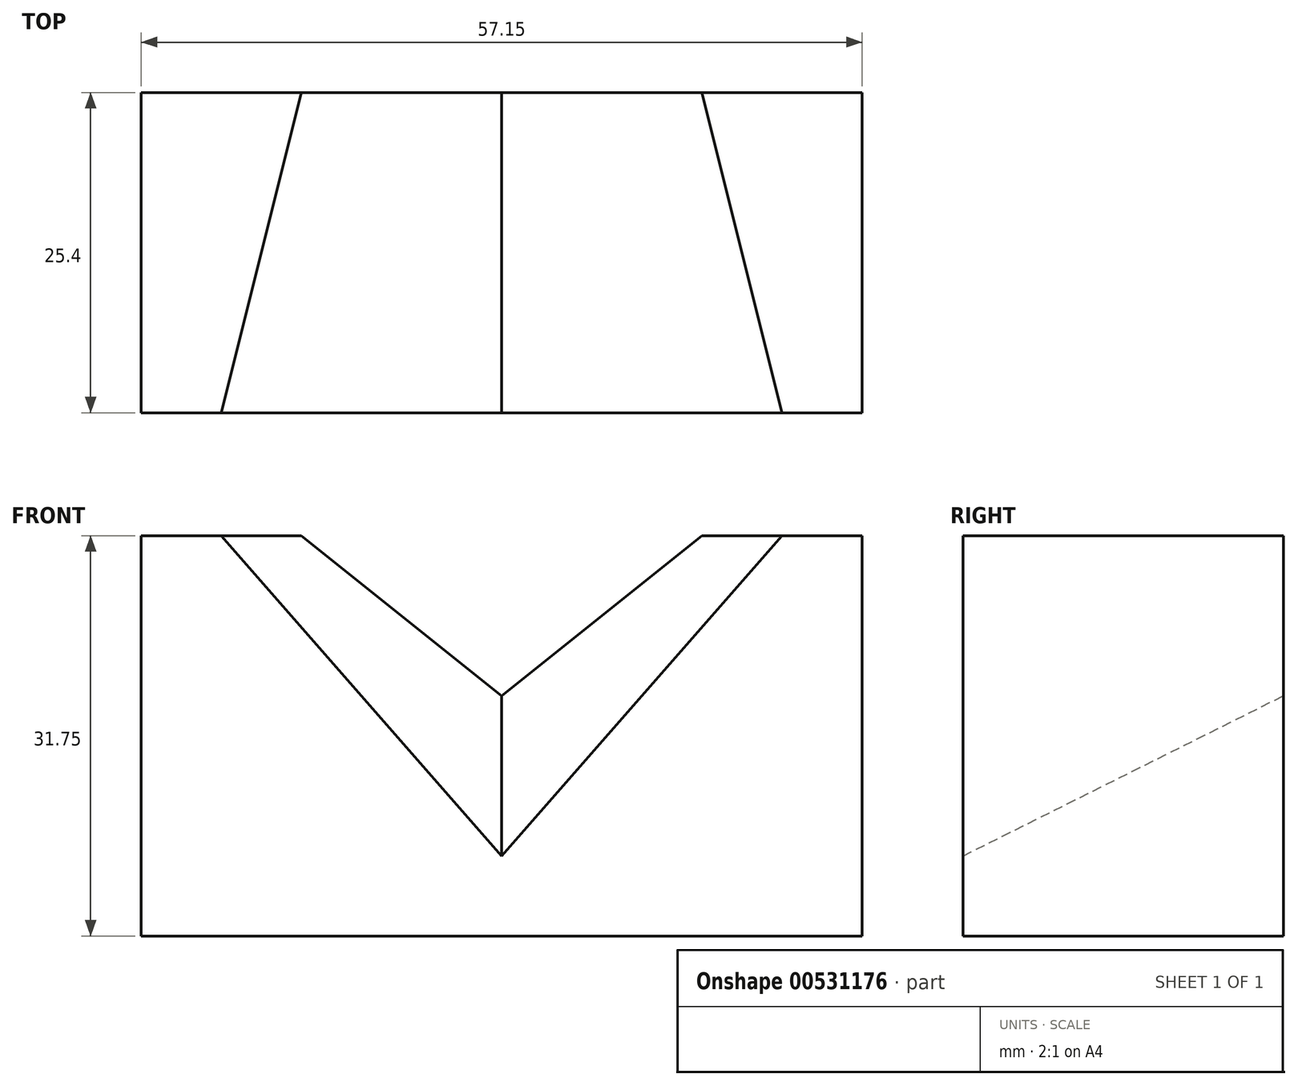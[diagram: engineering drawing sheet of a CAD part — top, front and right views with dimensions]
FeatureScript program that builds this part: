
annotation { "Feature Type Name" : "Feature", "Feature Type Description" : "" }
export const myFeature = defineFeature(function(context is Context, id is Id, definition is map)
    precondition{}
    {
        {
            var Q0;
            Q0=qCreatedBy(makeId("Front.planeOp"),FACE);
            var sketch = newSketch(context, id + "F0", { "sketchPlane" : qUnion([Q0])});
            skLineSegment(sketch, "E0", {"start": v(0, 0) * mm, "end": v(0, 31.75) * mm});
            skLineSegment(sketch, "E1", {"start": v(0, 31.75) * mm, "end": v(57.15, 31.75) * mm});
            skLineSegment(sketch, "E2", {"start": v(57.15, 31.75) * mm, "end": v(57.15, 0) * mm});
            skLineSegment(sketch, "E3", {"start": v(57.15, 0) * mm, "end": v(0, 0) * mm});
            skSolve(sketch);
        }
        {
            var Q0;
            Q0=makeQuery(id+"F0.imprint","IMPRINT",FACE,{"disambiguationData":[TD([[makeQuery(id+"F0.imprint","IMPRINT",EDGE,{"derivedFrom":sQuery(id+"F0.wireOp",EDGE,"E0")}),-1.0]])]});
            extrude(context, id + "F1", {"entities" : qUnion([Q0]), "depth" : 25.4 * mm, "offsetDistance" : 25.4 * mm});
        }
        {
            var Q0;
            Q0=qCreatedBy(makeId("Front.planeOp"),FACE);
            var sketch = newSketch(context, id + "F2", { "sketchPlane" : qUnion([Q0])});
            skLineSegment(sketch, "E4", {"start": v(0, 0) * mm, "end": v(0, 31.75) * mm});
            skLineSegment(sketch, "E5", {"start": v(0, 31.75) * mm, "end": v(12.7, 31.75) * mm});
            skLineSegment(sketch, "E6", {"start": v(0, 0) * mm, "end": v(28.58, 0) * mm});
            skLineSegment(sketch, "E7", {"start": v(28.58, 0) * mm, "end": v(28.58, 19.05) * mm});
            skLineSegment(sketch, "E8", {"start": v(28.58, 19.05) * mm, "end": v(12.7, 31.75) * mm});
            skLineSegment(sketch, "E9", {"start": v(28.58, 0) * mm, "end": v(57.15, 0) * mm});
            skLineSegment(sketch, "E10", {"start": v(57.15, 0) * mm, "end": v(57.15, 31.75) * mm});
            skLineSegment(sketch, "E11", {"start": v(57.15, 31.75) * mm, "end": v(44.45, 31.75) * mm});
            skLineSegment(sketch, "E12", {"start": v(44.45, 31.75) * mm, "end": v(28.58, 19.05) * mm});
            skLineSegment(sketch, "E13", {"start": v(12.7, 31.75) * mm, "end": v(44.45, 31.75) * mm});
            skSolve(sketch);
        }
        {
            var Q0;
            Q0=qCreatedBy(makeId("Front.planeOp"),FACE);
            cPlane(context, id + "F3", {"entities" : qUnion([Q0]), "cplaneType" : CPlaneType.OFFSET, "offset" : 25.4 * mm, "width" : 152.4 * mm, "height" : 152.4 * mm});
        }
        {
            var Q0;
            Q0=qCreatedBy(id+"F3.planeOp",FACE);
            var sketch = newSketch(context, id + "F4", { "sketchPlane" : qUnion([Q0])});
            skLineSegment(sketch, "E14", {"start": v(0, 0) * mm, "end": v(0, 31.75) * mm});
            skLineSegment(sketch, "E15", {"start": v(0, 31.75) * mm, "end": v(6.35, 31.75) * mm});
            skLineSegment(sketch, "E16", {"start": v(0, 0) * mm, "end": v(28.58, 0) * mm});
            skLineSegment(sketch, "E17", {"start": v(28.58, 0) * mm, "end": v(28.58, 6.35) * mm});
            skLineSegment(sketch, "E18", {"start": v(28.58, 6.35) * mm, "end": v(6.35, 31.75) * mm});
            skLineSegment(sketch, "E19", {"start": v(28.58, 0) * mm, "end": v(57.15, 0) * mm});
            skLineSegment(sketch, "E20", {"start": v(57.15, 0) * mm, "end": v(57.15, 31.75) * mm});
            skLineSegment(sketch, "E21", {"start": v(57.15, 31.75) * mm, "end": v(50.8, 31.75) * mm});
            skLineSegment(sketch, "E22", {"start": v(50.8, 31.75) * mm, "end": v(28.58, 6.35) * mm});
            skLineSegment(sketch, "E23", {"start": v(50.8, 31.75) * mm, "end": v(6.35, 31.75) * mm});
            skSolve(sketch);
        }
        {
            var Q1;
            Q1=makeQuery(id+"F4.imprint","IMPRINT",FACE,{"disambiguationData":[TD([[makeQuery(id+"F4.imprint","IMPRINT",EDGE,{"derivedFrom":sQuery(id+"F4.wireOp",EDGE,"E18")}),-1.0]])]});
            var Q2;
            Q2=makeQuery(id+"F2.imprint","IMPRINT",FACE,{"disambiguationData":[TD([[makeQuery(id+"F2.imprint","IMPRINT",EDGE,{"derivedFrom":sQuery(id+"F2.wireOp",EDGE,"E8")}),-1.0]])]});
            loft(context, id + "F5", {"operationType" : NewBodyOperationType.REMOVE, "sheetProfilesArray" : [{ "sheetProfileEntities" : qUnion([Q1]) }, { "sheetProfileEntities" : qUnion([Q2]) }]});
        }
    });
